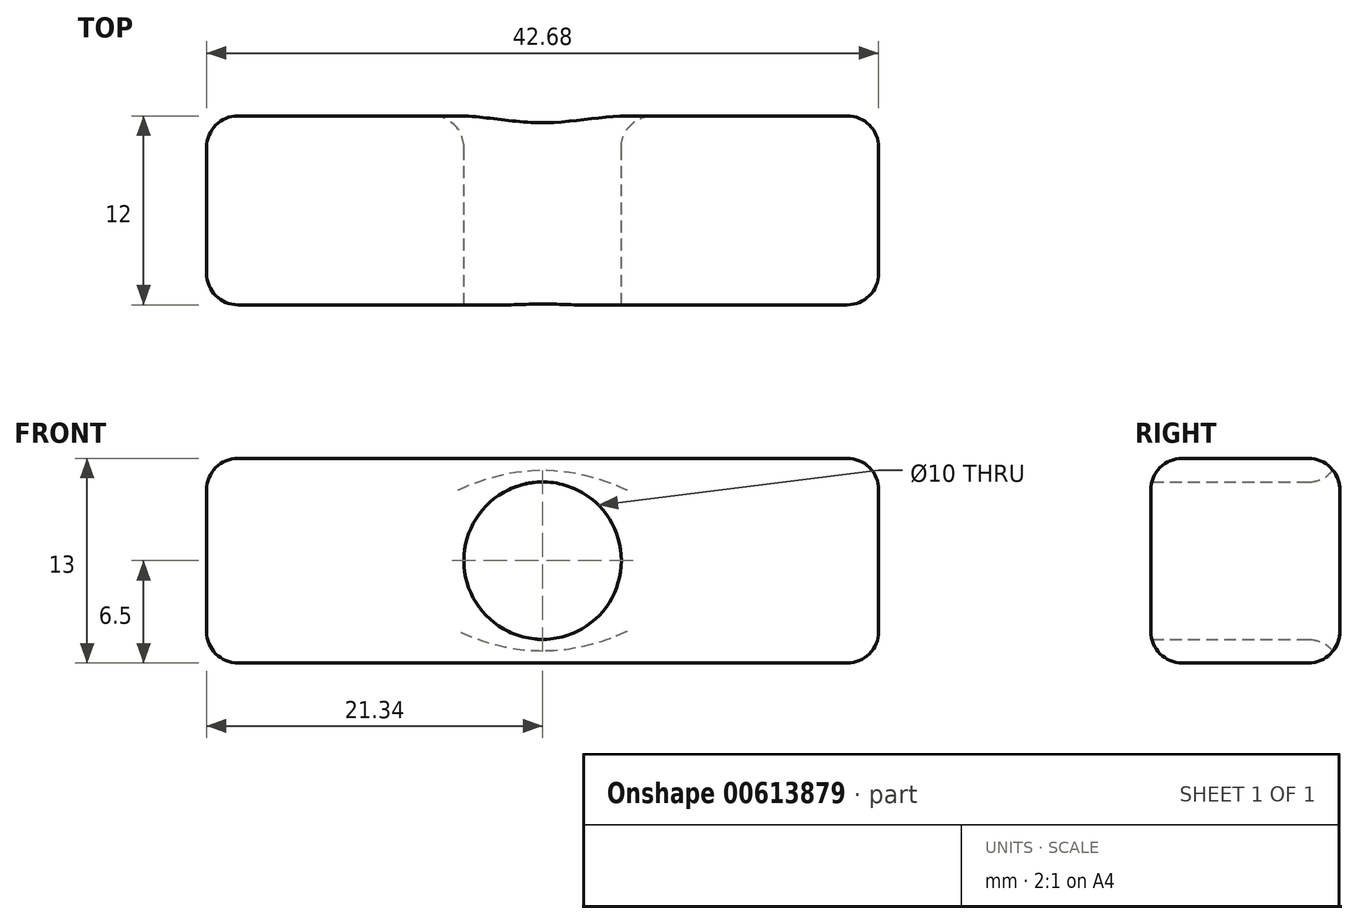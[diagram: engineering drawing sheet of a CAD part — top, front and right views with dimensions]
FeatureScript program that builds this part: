
annotation { "Feature Type Name" : "Feature", "Feature Type Description" : "" }
export const myFeature = defineFeature(function(context is Context, id is Id, definition is map)
    precondition{}
    {
        {
            var Q0;
            Q0=qCreatedBy(makeId("Front.planeOp"),FACE);
            var sketch = newSketch(context, id + "F0", { "sketchPlane" : qUnion([Q0])});
            skLineSegment(sketch, "E0.bottom", {"start": v(-21.34, 6.5) * mm, "end": v(21.34, 6.5) * mm});
            skLineSegment(sketch, "E0.top", {"start": v(-21.34, -6.5) * mm, "end": v(21.34, -6.5) * mm});
            skLineSegment(sketch, "E0.left", {"start": v(-21.34, 6.5) * mm, "end": v(-21.34, -6.5) * mm});
            skLineSegment(sketch, "E0.right", {"start": v(21.34, 6.5) * mm, "end": v(21.34, -6.5) * mm});
            skPoint(sketch, "E0.middle", {"position": v(0, 0) * mm});
            skCircle(sketch, "E1", {"center": v(0, 0) * mm, "radius": 5 * mm});
            skSolve(sketch);
        }
        {
            var Q0;
            Q0=makeQuery(id+"F0.imprint","IMPRINT",FACE,{"disambiguationData":[TD([[makeQuery(id+"F0.imprint","IMPRINT",EDGE,{"derivedFrom":sQuery(id+"F0.wireOp",EDGE,"E0.bottom")}),-1.0]])]});
            extrude(context, id + "F1", {"entities" : qUnion([Q0]), "depth" : 12 * mm, "offsetDistance" : 25 * mm});
        }
        {
            var Q0;
            Q0=makeQuery(id+"F1.opExtrude","SWEPT_EDGE",EDGE,{"disambiguationData":[OSD([sQuery(id+"F0.wireOp",EDGE,"E0.bottom"),sQuery(id+"F0.wireOp",EDGE,"E0.left")])]});
            var Q1;
            Q1=makeQuery(id+"F1.opExtrude","SWEPT_EDGE",EDGE,{"disambiguationData":[OSD([sQuery(id+"F0.wireOp",EDGE,"E0.bottom"),sQuery(id+"F0.wireOp",EDGE,"E0.right")])]});
            var Q2;
            Q2=makeQuery(id+"F1.opExtrude","SWEPT_EDGE",EDGE,{"disambiguationData":[OSD([sQuery(id+"F0.wireOp",EDGE,"E0.top"),sQuery(id+"F0.wireOp",EDGE,"E0.right")])]});
            var Q3;
            Q3=makeQuery(id+"F1.opExtrude","CAP_EDGE",EDGE,{"disambiguationData":[OSD([sQuery(id+"F0.wireOp",EDGE,"E0.right")])],"isStart":false});
            var Q4;
            Q4=makeQuery(id+"F1.opExtrude","CAP_EDGE",EDGE,{"disambiguationData":[OSD([sQuery(id+"F0.wireOp",EDGE,"E0.bottom")])],"isStart":true});
            var Q5;
            Q5=makeQuery(id+"F1.opExtrude","CAP_EDGE",EDGE,{"disambiguationData":[OSD([sQuery(id+"F0.wireOp",EDGE,"E0.bottom")])],"isStart":false});
            var Q6;
            Q6=makeQuery(id+"F1.opExtrude","CAP_EDGE",EDGE,{"disambiguationData":[OSD([sQuery(id+"F0.wireOp",EDGE,"E0.right")])],"isStart":true});
            var Q7;
            Q7=makeQuery(id+"F1.opExtrude","CAP_EDGE",EDGE,{"disambiguationData":[OSD([sQuery(id+"F0.wireOp",EDGE,"E0.left")])],"isStart":false});
            var Q8;
            Q8=makeQuery(id+"F1.opExtrude","SWEPT_EDGE",EDGE,{"disambiguationData":[OSD([sQuery(id+"F0.wireOp",EDGE,"E0.top"),sQuery(id+"F0.wireOp",EDGE,"E0.left")])]});
            var Q9;
            Q9=makeQuery(id+"F1.opExtrude","CAP_EDGE",EDGE,{"disambiguationData":[OSD([sQuery(id+"F0.wireOp",EDGE,"E0.top")])],"isStart":true});
            var Q10;
            Q10=makeQuery(id+"F1.opExtrude","CAP_EDGE",EDGE,{"disambiguationData":[OSD([sQuery(id+"F0.wireOp",EDGE,"E0.top")])],"isStart":false});
            var Q11;
            Q11=makeQuery(id+"F1.opExtrude","CAP_EDGE",EDGE,{"disambiguationData":[OSD([sQuery(id+"F0.wireOp",EDGE,"E0.left")])],"isStart":true});
            var Q12;
            Q12=makeQuery(id+"F1.opExtrude","CAP_EDGE",EDGE,{"disambiguationData":[OSD([sQuery(id+"F0.wireOp",EDGE,"E1")])],"isStart":true});
            fillet(context, id + "F2", {"entities" : qUnion([Q0, Q1, Q2, Q3, Q4, Q5, Q6, Q7, Q8, Q9, Q10, Q11, Q12]), "radius" : 2 * mm, "tangentPropagation" : true, "allowEdgeOverflow" : false});
        }
    });
